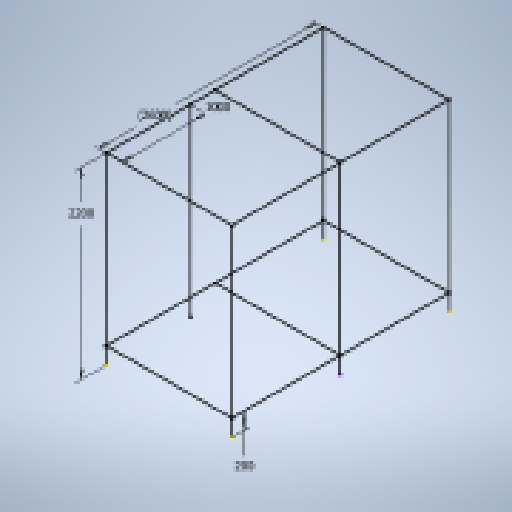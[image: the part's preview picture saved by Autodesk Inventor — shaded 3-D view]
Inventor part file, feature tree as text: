
AUTODESK INVENTOR PART (.ipt)
format: ipt  version: 2025 (Build 290162010, 162A)  size: 144,896 bytes
history: native  units: mm
features: sketch x2
ambient origin geometry x8: Origin, YZ Plane, XZ Plane, XY Plane, X Axis, Y Axis, Z Axis, Center Point
feature tree (2):
  sketch  "Sketch1"  dims[d0=1500.0mm d1=2600.0mm d4=2200.0mm d5=200.0mm d6=2600.0mm d7=1000.0mm]
  sketch  "3D Sketch2"
